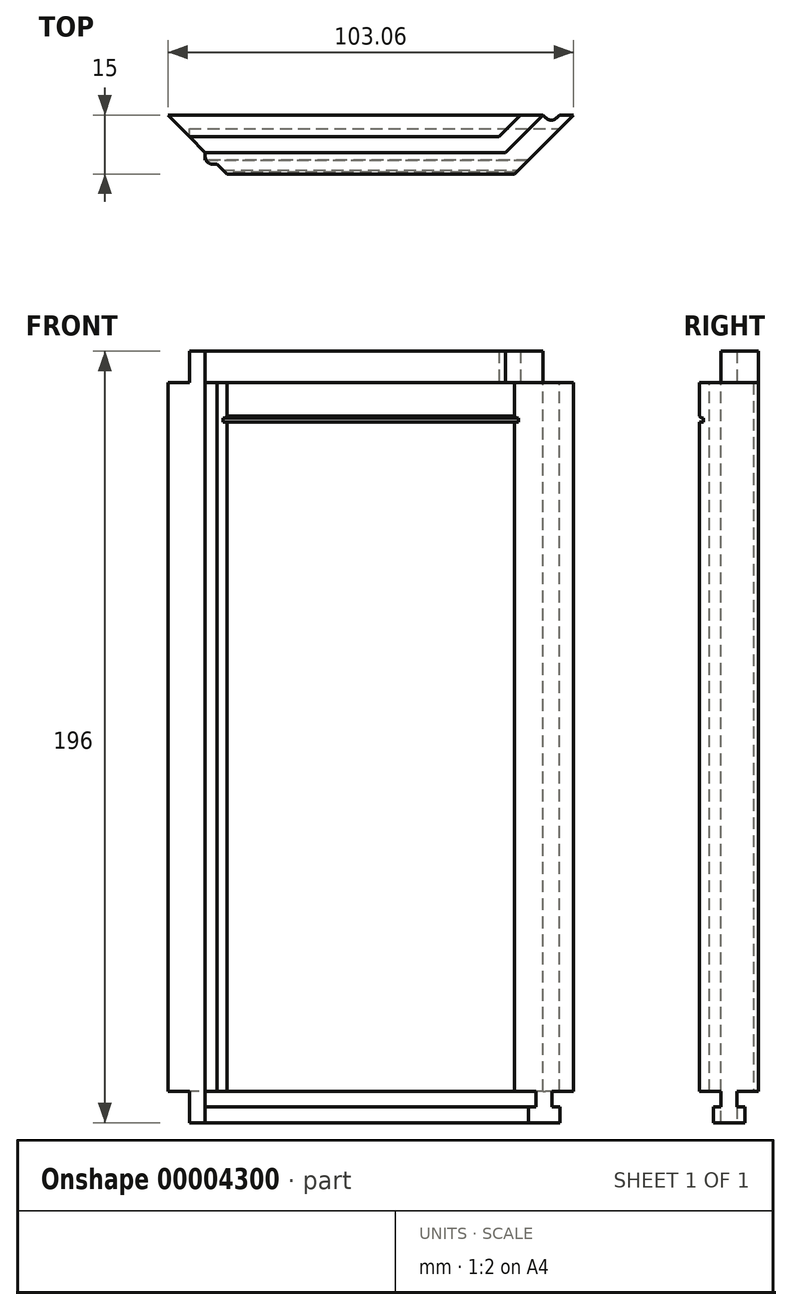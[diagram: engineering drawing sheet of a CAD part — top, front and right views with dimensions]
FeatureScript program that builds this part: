
annotation { "Feature Type Name" : "Feature", "Feature Type Description" : "" }
export const myFeature = defineFeature(function(context is Context, id is Id, definition is map)
    precondition{}
    {
        {
            var Q0;
            Q0=qCreatedBy(makeId("Front.planeOp"),FACE);
            var sketch = newSketch(context, id + "F0", { "sketchPlane" : qUnion([Q0])});
            skLineSegment(sketch, "E0", {"start": v(-65.43, 150.4) * mm, "end": v(37.63, 150.4) * mm});
            skLineSegment(sketch, "E1", {"start": v(37.63, 150.4) * mm, "end": v(37.63, -29.6) * mm});
            skLineSegment(sketch, "E2", {"start": v(37.63, -29.6) * mm, "end": v(-65.43, -29.6) * mm});
            skLineSegment(sketch, "E3", {"start": v(-65.43, -29.6) * mm, "end": v(-65.43, 150.4) * mm});
            skSolve(sketch);
        }
        {
            var Q0;
            Q0=makeQuery(id+"F0.imprint","IMPRINT",FACE,{"disambiguationData":[TD([[makeQuery(id+"F0.imprint","IMPRINT",EDGE,{"derivedFrom":sQuery(id+"F0.wireOp",EDGE,"E0")}),-1.0]])]});
            extrude(context, id + "F1", {"entities" : qUnion([Q0]), "depth" : 15 * mm});
        }
        {
            var Q0;
            Q0=makeQuery(id+"F1.opExtrude","SWEPT_FACE",FACE,{"disambiguationData":[OSD([sQuery(id+"F0.wireOp",EDGE,"E2")])]});
            var sketch = newSketch(context, id + "F2", { "sketchPlane" : qUnion([Q0])});
            skLineSegment(sketch, "E4", {"start": v(-65.43, 15) * mm, "end": v(-65.43, 0) * mm});
            skLineSegment(sketch, "E5", {"start": v(-65.43, 0) * mm, "end": v(37.63, 0) * mm});
            skLineSegment(sketch, "E6", {"start": v(37.63, 0) * mm, "end": v(37.63, 15) * mm});
            skLineSegment(sketch, "E7", {"start": v(37.63, 15) * mm, "end": v(-65.43, 15) * mm});
            skLineSegment(sketch, "E8.0", {"start": v(37.63, 9.5) * mm, "end": v(-65.43, 9.5) * mm});
            skLineSegment(sketch, "E9.0", {"start": v(-65.43, 5.5) * mm, "end": v(37.63, 5.5) * mm});
            skSolve(sketch);
        }
        {
            var Q0;
            {var subQ1=sQuery(id+"F2.wireOp",EDGE,"E8.0");Q0=makeQuery(id+"F2.imprint","IMPRINT",FACE,{"disambiguationData":[TD([[makeQuery(id+"F2.imprint","IMPRINT",EDGE,{"derivedFrom":subQ1}),1.0]])]});}
            extrude(context, id + "F3", {"entities" : qUnion([Q0]), "operationType" : NewBodyOperationType.ADD, "depth" : 8 * mm});
        }
        {
            var Q0;
            Q0=makeQuery(id+"F3.opExtrude","SWEPT_FACE",FACE,{"disambiguationData":[OSD([sQuery(id+"F2.wireOp",EDGE,"E8.0")])]});
            var sketch = newSketch(context, id + "F4", { "sketchPlane" : qUnion([Q0])});
            skLineSegment(sketch, "E10", {"start": v(-65.43, -29.6) * mm, "end": v(-65.43, -37.6) * mm});
            skLineSegment(sketch, "E11", {"start": v(-65.43, -37.6) * mm, "end": v(37.63, -37.6) * mm});
            skLineSegment(sketch, "E12", {"start": v(37.63, -37.6) * mm, "end": v(37.63, -29.6) * mm});
            skLineSegment(sketch, "E13", {"start": v(37.63, -29.6) * mm, "end": v(-65.43, -29.6) * mm});
            skLineSegment(sketch, "E14.0", {"start": v(-65.43, -33.6) * mm, "end": v(37.63, -33.6) * mm});
            skSolve(sketch);
        }
        {
            var Q0;
            {var subQ2=sQuery(id+"F4.wireOp",EDGE,"E11");Q0=makeQuery(id+"F4.imprint","IMPRINT",FACE,{"disambiguationData":[TD([[makeQuery(id+"F4.imprint","IMPRINT",EDGE,{"derivedFrom":subQ2}),-1.0]])]});}
            extrude(context, id + "F5", {"entities" : qUnion([Q0]), "operationType" : NewBodyOperationType.ADD, "depth" : 2 * mm});
        }
        {
            var Q0;
            Q0=makeQuery(id+"F3.opExtrude","SWEPT_FACE",FACE,{"disambiguationData":[OSD([sQuery(id+"F2.wireOp",EDGE,"E9.0")])]});
            var sketch = newSketch(context, id + "F6", { "sketchPlane" : qUnion([Q0])});
            skLineSegment(sketch, "E15", {"start": v(65.43, -37.6) * mm, "end": v(-37.63, -37.6) * mm});
            skLineSegment(sketch, "E16", {"start": v(-37.63, -37.6) * mm, "end": v(-37.63, -29.6) * mm});
            skLineSegment(sketch, "E17", {"start": v(65.43, -37.6) * mm, "end": v(65.43, -29.6) * mm});
            skLineSegment(sketch, "E18.0", {"start": v(65.43, -33.6) * mm, "end": v(-37.63, -33.6) * mm});
            skSolve(sketch);
        }
        {
            var Q0;
            {var subQ2=sQuery(id+"F6.wireOp",EDGE,"E15");Q0=makeQuery(id+"F6.imprint","IMPRINT",FACE,{"disambiguationData":[TD([[makeQuery(id+"F6.imprint","IMPRINT",EDGE,{"derivedFrom":subQ2}),-1.0]])]});}
            extrude(context, id + "F7", {"entities" : qUnion([Q0]), "operationType" : NewBodyOperationType.ADD, "depth" : 2 * mm});
        }
        {
            var Q0;
            Q0=makeQuery(id+"F1.opExtrude","SWEPT_FACE",FACE,{"disambiguationData":[OSD([sQuery(id+"F0.wireOp",EDGE,"E0")])]});
            var sketch = newSketch(context, id + "F8", { "sketchPlane" : qUnion([Q0])});
            skLineSegment(sketch, "E19", {"start": v(-65.43, 0) * mm, "end": v(-65.43, -15) * mm});
            skLineSegment(sketch, "E20", {"start": v(-65.43, -15) * mm, "end": v(37.63, -15) * mm});
            skLineSegment(sketch, "E21", {"start": v(37.63, -15) * mm, "end": v(37.63, 0) * mm});
            skLineSegment(sketch, "E22", {"start": v(37.63, 0) * mm, "end": v(-65.43, 0) * mm});
            skLineSegment(sketch, "E23.0", {"start": v(-50.43, 0) * mm, "end": v(-50.43, -15) * mm});
            skLineSegment(sketch, "E24.0", {"start": v(22.63, -15) * mm, "end": v(22.63, 0) * mm});
            skLineSegment(sketch, "E25", {"start": v(-65.43, 0) * mm, "end": v(-50.43, -15) * mm});
            skLineSegment(sketch, "E26", {"start": v(37.63, 0) * mm, "end": v(22.63, -15) * mm});
            skSolve(sketch);
        }
        {
            var Q0;
            {var subQ2=sQuery(id+"F8.wireOp",EDGE,"E19");Q0=makeQuery(id+"F8.imprint","IMPRINT",FACE,{"disambiguationData":[TD([[makeQuery(id+"F8.imprint","IMPRINT",EDGE,{"derivedFrom":subQ2}),-1.0]])]});}
            var Q1;
            {var subQ1=sQuery(id+"F8.wireOp",EDGE,"E21");Q1=makeQuery(id+"F8.imprint","IMPRINT",FACE,{"disambiguationData":[TD([[makeQuery(id+"F8.imprint","IMPRINT",EDGE,{"derivedFrom":subQ1}),1.0]])]});}
            extrude(context, id + "F9", {"entities" : qUnion([Q0, Q1]), "operationType" : NewBodyOperationType.REMOVE, "oppositeDirection" : true, "depth" : 212.57 * mm});
        }
        {
            var Q0;
            Q0=makeQuery(id+"F7.boolean.opBoolean","MERGE",FACE,{"derivedFrom":[makeQuery(id+"F5.boolean.opBoolean","MERGE",FACE,{"derivedFrom":[makeQuery(id+"F3.opExtrude","CAP_FACE",FACE,{"disambiguationData":[OSD([sQuery(id+"F2.wireOp",EDGE,"E4"),sQuery(id+"F2.wireOp",EDGE,"E6"),sQuery(id+"F2.wireOp",EDGE,"E8.0"),sQuery(id+"F2.wireOp",EDGE,"E9.0")])],"isStart":false}),makeQuery(id+"F5.opExtrude","SWEPT_FACE",FACE,{"disambiguationData":[OSD([sQuery(id+"F4.wireOp",EDGE,"E11")])]})]}),makeQuery(id+"F7.opExtrude","SWEPT_FACE",FACE,{"disambiguationData":[OSD([sQuery(id+"F6.wireOp",EDGE,"E15")])]})]});
            var sketch = newSketch(context, id + "F10", { "sketchPlane" : qUnion([Q0])});
            skLineSegment(sketch, "E27", {"start": v(-61.93, 3.5) * mm, "end": v(-59.93, 3.5) * mm});
            skLineSegment(sketch, "E28", {"start": v(-61.93, 3.5) * mm, "end": v(-56.17, 9.26) * mm});
            skLineSegment(sketch, "E29.0", {"start": v(-59.93, 5.5) * mm, "end": v(-59.93, 3.5) * mm});
            skLineSegment(sketch, "E30", {"start": v(-61.93, 3.5) * mm, "end": v(-59.93, 5.5) * mm});
            skLineSegment(sketch, "E31", {"start": v(-53.93, 11.5) * mm, "end": v(-53.93, 9.5) * mm});
            skLineSegment(sketch, "E32.0", {"start": v(-55.93, 9.5) * mm, "end": v(-53.93, 9.5) * mm});
            skLineSegment(sketch, "E33", {"start": v(-53.93, 11.5) * mm, "end": v(-55.93, 9.5) * mm});
            skLineSegment(sketch, "E34.trimOffspring", {"start": v(-55.93, 9.5) * mm, "end": v(-53.93, 11.5) * mm});
            skSolve(sketch);
        }
        {
            var Q0;
            Q0=makeQuery(id+"F10.imprint","IMPRINT",FACE,{"disambiguationData":[TD([[makeQuery(id+"F10.imprint","IMPRINT",EDGE,{"derivedFrom":sQuery(id+"F10.wireOp",EDGE,"E27")}),1.0]])]});
            var Q1;
            Q1=makeQuery(id+"F10.imprint","IMPRINT",FACE,{"disambiguationData":[TD([[makeQuery(id+"F10.imprint","IMPRINT",EDGE,{"derivedFrom":sQuery(id+"F10.wireOp",EDGE,"E31")}),-1.0]])]});
            extrude(context, id + "F11", {"entities" : qUnion([Q0, Q1]), "operationType" : NewBodyOperationType.REMOVE, "oppositeDirection" : true, "depth" : 4 * mm});
        }
        {
            var Q0;
            Q0=makeQuery(id+"F11.boolean.opBoolean","COPY",FACE,{"derivedFrom":makeQuery(id+"F11.opExtrude","SWEPT_FACE",FACE,{"disambiguationData":[OSD([sQuery(id+"F10.wireOp",EDGE,"E31")])]})});
            extrude(context, id + "F12", {"entities" : qUnion([Q0]), "operationType" : NewBodyOperationType.ADD, "depth" : 2 * mm});
        }
        {
            var Q0;
            Q0=makeQuery(id+"F1.opExtrude","SWEPT_FACE",FACE,{"disambiguationData":[OSD([sQuery(id+"F0.wireOp",EDGE,"E0")])]});
            var sketch = newSketch(context, id + "F13", { "sketchPlane" : qUnion([Q0])});
            skLineSegment(sketch, "E35", {"start": v(37.63, 0) * mm, "end": v(-65.43, 0) * mm});
            skLineSegment(sketch, "E36", {"start": v(-65.43, 0) * mm, "end": v(-50.43, -15) * mm});
            skLineSegment(sketch, "E37", {"start": v(-50.43, -15) * mm, "end": v(22.63, -15) * mm});
            skLineSegment(sketch, "E38", {"start": v(22.63, -15) * mm, "end": v(37.63, 0) * mm});
            skLineSegment(sketch, "E39.0", {"start": v(20.35, -9.5) * mm, "end": v(-55.93, -9.5) * mm});
            skLineSegment(sketch, "E40.0", {"start": v(20.35, -9.5) * mm, "end": v(29.85, 0) * mm});
            skLineSegment(sketch, "E41.0", {"start": v(18.7, -5.5) * mm, "end": v(24.2, 0) * mm});
            skLineSegment(sketch, "E42.trimOffspring", {"start": v(18.7, -5.5) * mm, "end": v(-59.93, -5.5) * mm});
            skSolve(sketch);
        }
        {
            var Q0;
            {var subQ3=sQuery(id+"F13.wireOp",EDGE,"E39.0");Q0=makeQuery(id+"F13.imprint","IMPRINT",FACE,{"disambiguationData":[TD([[makeQuery(id+"F13.imprint","IMPRINT",EDGE,{"derivedFrom":subQ3}),-1.0]])]});}
            extrude(context, id + "F14", {"entities" : qUnion([Q0]), "operationType" : NewBodyOperationType.ADD, "depth" : 8 * mm});
        }
        {
            var Q0;
            Q0=makeQuery(id+"F1.opExtrude","CAP_FACE",FACE,{"disambiguationData":[OSD([sQuery(id+"F0.wireOp",EDGE,"E0"),sQuery(id+"F0.wireOp",EDGE,"E1"),sQuery(id+"F0.wireOp",EDGE,"E2"),sQuery(id+"F0.wireOp",EDGE,"E3")])],"isStart":false});
            var sketch = newSketch(context, id + "F15", { "sketchPlane" : qUnion([Q0])});
            skLineSegment(sketch, "E43.0", {"start": v(-50.43, 140.4) * mm, "end": v(22.63, 140.4) * mm});
            skLineSegment(sketch, "E44.0", {"start": v(-50.43, 141.4) * mm, "end": v(22.63, 141.4) * mm});
            skSolve(sketch);
        }
        {
            var Q0;
            {var subQ3=sQuery(id+"F15.wireOp",EDGE,"E43.0");Q0=makeQuery(id+"F15.imprint","IMPRINT",FACE,{"disambiguationData":[TD([[makeQuery(id+"F15.imprint","IMPRINT",EDGE,{"derivedFrom":subQ3}),1.0]])]});}
            extrude(context, id + "F16", {"entities" : qUnion([Q0]), "operationType" : NewBodyOperationType.REMOVE, "oppositeDirection" : true, "depth" : 1 * mm});
        }
        {
            var Q0;
            Q0=makeQuery(id+"F16.boolean.opBoolean","COPY",EDGE,{"derivedFrom":makeQuery(id+"F16.opExtrude","CAP_EDGE",EDGE,{"disambiguationData":[OSD([sQuery(id+"F15.wireOp",EDGE,"E44.0")])],"isStart":true})});
            var Q1;
            Q1=makeQuery(id+"F16.boolean.opBoolean","COPY",EDGE,{"derivedFrom":makeQuery(id+"F16.opExtrude","CAP_EDGE",EDGE,{"disambiguationData":[OSD([sQuery(id+"F15.wireOp",EDGE,"E43.0")])],"isStart":true})});
            chamfer(context, id + "F17", {"entities" : qUnion([Q0, Q1]), "width" : 0.5 * mm, "tangentPropagation" : true});
        }
        {
            var Q0;
            Q0=makeQuery(id+"F16.boolean.opBoolean","COPY",FACE,{"derivedFrom":makeQuery(id+"F16.opExtrude","SWEPT_FACE",FACE,{"disambiguationData":[OSD([sQuery(id+"F8.wireOp",EDGE,"E20"),sQuery(id+"F8.wireOp",EDGE,"E23.0"),sQuery(id+"F8.wireOp",EDGE,"E25")])]})});
            extrude(context, id + "F18", {"entities" : qUnion([Q0]), "operationType" : NewBodyOperationType.REMOVE, "oppositeDirection" : true, "depth" : 25 * mm});
        }
        {
            var Q0;
            Q0=makeQuery(id+"F16.boolean.opBoolean","COPY",FACE,{"derivedFrom":makeQuery(id+"F16.opExtrude","SWEPT_FACE",FACE,{"disambiguationData":[OSD([sQuery(id+"F8.wireOp",EDGE,"E20"),sQuery(id+"F8.wireOp",EDGE,"E24.0"),sQuery(id+"F8.wireOp",EDGE,"E26")])]})});
            extrude(context, id + "F19", {"entities" : qUnion([Q0]), "operationType" : NewBodyOperationType.REMOVE, "oppositeDirection" : true, "depth" : 25 * mm});
        }
        {
            var Q0;
            {var subQ0=sQuery(id+"F0.wireOp",EDGE,"E0");Q0=makeQuery(id+"F14.boolean.opBoolean","SPLIT",FACE,{"disambiguationData":[TD([makeQuery(id+"F9.boolean.opBoolean","COPY",FACE,{"derivedFrom":makeQuery(id+"F9.opExtrude","SWEPT_FACE",FACE,{"disambiguationData":[OSD([sQuery(id+"F8.wireOp",EDGE,"E26")])]})})])],"derivedFrom":makeQuery(id+"F1.opExtrude","SWEPT_FACE",FACE,{"disambiguationData":[OSD([subQ0])]})});}
            var sketch = newSketch(context, id + "F20", { "sketchPlane" : qUnion([Q0])});
            skLineSegment(sketch, "E45", {"start": v(7.48, 0) * mm, "end": v(37.63, 0) * mm});
            skLineSegment(sketch, "E46.0", {"start": v(22.47, -11.62) * mm, "end": v(34.1, 0) * mm});
            skLineSegment(sketch, "E47.0", {"start": v(26.85, -3) * mm, "end": v(37.63, -3) * mm});
            skLineSegment(sketch, "E48", {"start": v(29.85, 0) * mm, "end": v(24.13, -5.72) * mm});
            skLineSegment(sketch, "E49", {"start": v(17.22, 12.63) * mm, "end": v(31.97, -2.12) * mm});
            skLineSegment(sketch, "E50.0", {"start": v(23.35, 6.5) * mm, "end": v(14.73, -2.12) * mm});
            skLineSegment(sketch, "E51.0", {"start": v(10.72, 6.13) * mm, "end": v(25.47, -8.62) * mm});
            skLineSegment(sketch, "E52", {"start": v(14.73, -2.12) * mm, "end": v(12.61, 0) * mm});
            skSolve(sketch);
        }
        {
            var Q0;
            {var subQ0=sQuery(id+"F20.wireOp",EDGE,"E48");var subQ3=sQuery(id+"F20.wireOp",EDGE,"E45");var subQ4=makeQuery(id+"F20.imprint","INTERSECT",VERTEX,{"derivedFrom":[subQ3,subQ0]});Q0=makeQuery(id+"F20.imprint","IMPRINT",FACE,{"disambiguationData":[TD([[makeQuery(id+"F20.imprint","IMPRINT",EDGE,{"disambiguationData":[TD([[subQ4,-1.0]])],"derivedFrom":subQ3}),-1.0]])]});}
            extrude(context, id + "F21", {"entities" : qUnion([Q0]), "operationType" : NewBodyOperationType.REMOVE, "oppositeDirection" : true, "depth" : 180 * mm});
        }
        {
            var Q0;
            {var subQ0=sQuery(id+"F0.wireOp",EDGE,"E0");Q0=makeQuery(id+"F14.boolean.opBoolean","SPLIT",FACE,{"disambiguationData":[TD([makeQuery(id+"F9.boolean.opBoolean","COPY",FACE,{"derivedFrom":makeQuery(id+"F9.opExtrude","SWEPT_FACE",FACE,{"disambiguationData":[OSD([sQuery(id+"F8.wireOp",EDGE,"E26")])]})})])],"derivedFrom":makeQuery(id+"F1.opExtrude","SWEPT_FACE",FACE,{"disambiguationData":[OSD([subQ0])]})});}
            var sketch = newSketch(context, id + "F22", { "sketchPlane" : qUnion([Q0])});
            skLineSegment(sketch, "E53.0", {"start": v(20.35, -12.5) * mm, "end": v(-55.93, -12.5) * mm});
            skLineSegment(sketch, "E54", {"start": v(-55.93, -9.5) * mm, "end": v(-52.93, -12.5) * mm});
            skLineSegment(sketch, "E55", {"start": v(-55.93, -12.5) * mm, "end": v(-55.93, -9.5) * mm});
            skSolve(sketch);
        }
        {
            var Q0;
            {var subQ1=sQuery(id+"F22.wireOp",EDGE,"E54");Q0=makeQuery(id+"F22.imprint","IMPRINT",FACE,{"disambiguationData":[TD([[makeQuery(id+"F22.imprint","IMPRINT",EDGE,{"derivedFrom":subQ1}),-1.0]])]});}
            extrude(context, id + "F23", {"entities" : qUnion([Q0]), "operationType" : NewBodyOperationType.ADD, "oppositeDirection" : true, "depth" : 180 * mm});
        }
        {
            var Q0;
            Q0=makeQuery(id+"F23.opExtrude","SWEPT_EDGE",EDGE,{"disambiguationData":[OSD([sQuery(id+"F22.wireOp",EDGE,"E53.0"),sQuery(id+"F22.wireOp",EDGE,"E55")])]});
            fillet(context, id + "F24", {"entities" : qUnion([Q0]), "radius" : 2 * mm, "tangentPropagation" : true, "allowEdgeOverflow" : false});
        }
        {
            var Q0;
            Q0=makeQuery(id+"F21.boolean.opBoolean","COPY",EDGE,{"derivedFrom":makeQuery(id+"F21.opExtrude","SWEPT_EDGE",EDGE,{"disambiguationData":[OSD([sQuery(id+"F20.wireOp",EDGE,"E46.0"),sQuery(id+"F20.wireOp",EDGE,"E49")])]})});
            fillet(context, id + "F25", {"entities" : qUnion([Q0]), "radius" : 2 * mm, "tangentPropagation" : true, "allowEdgeOverflow" : false});
        }
    });
